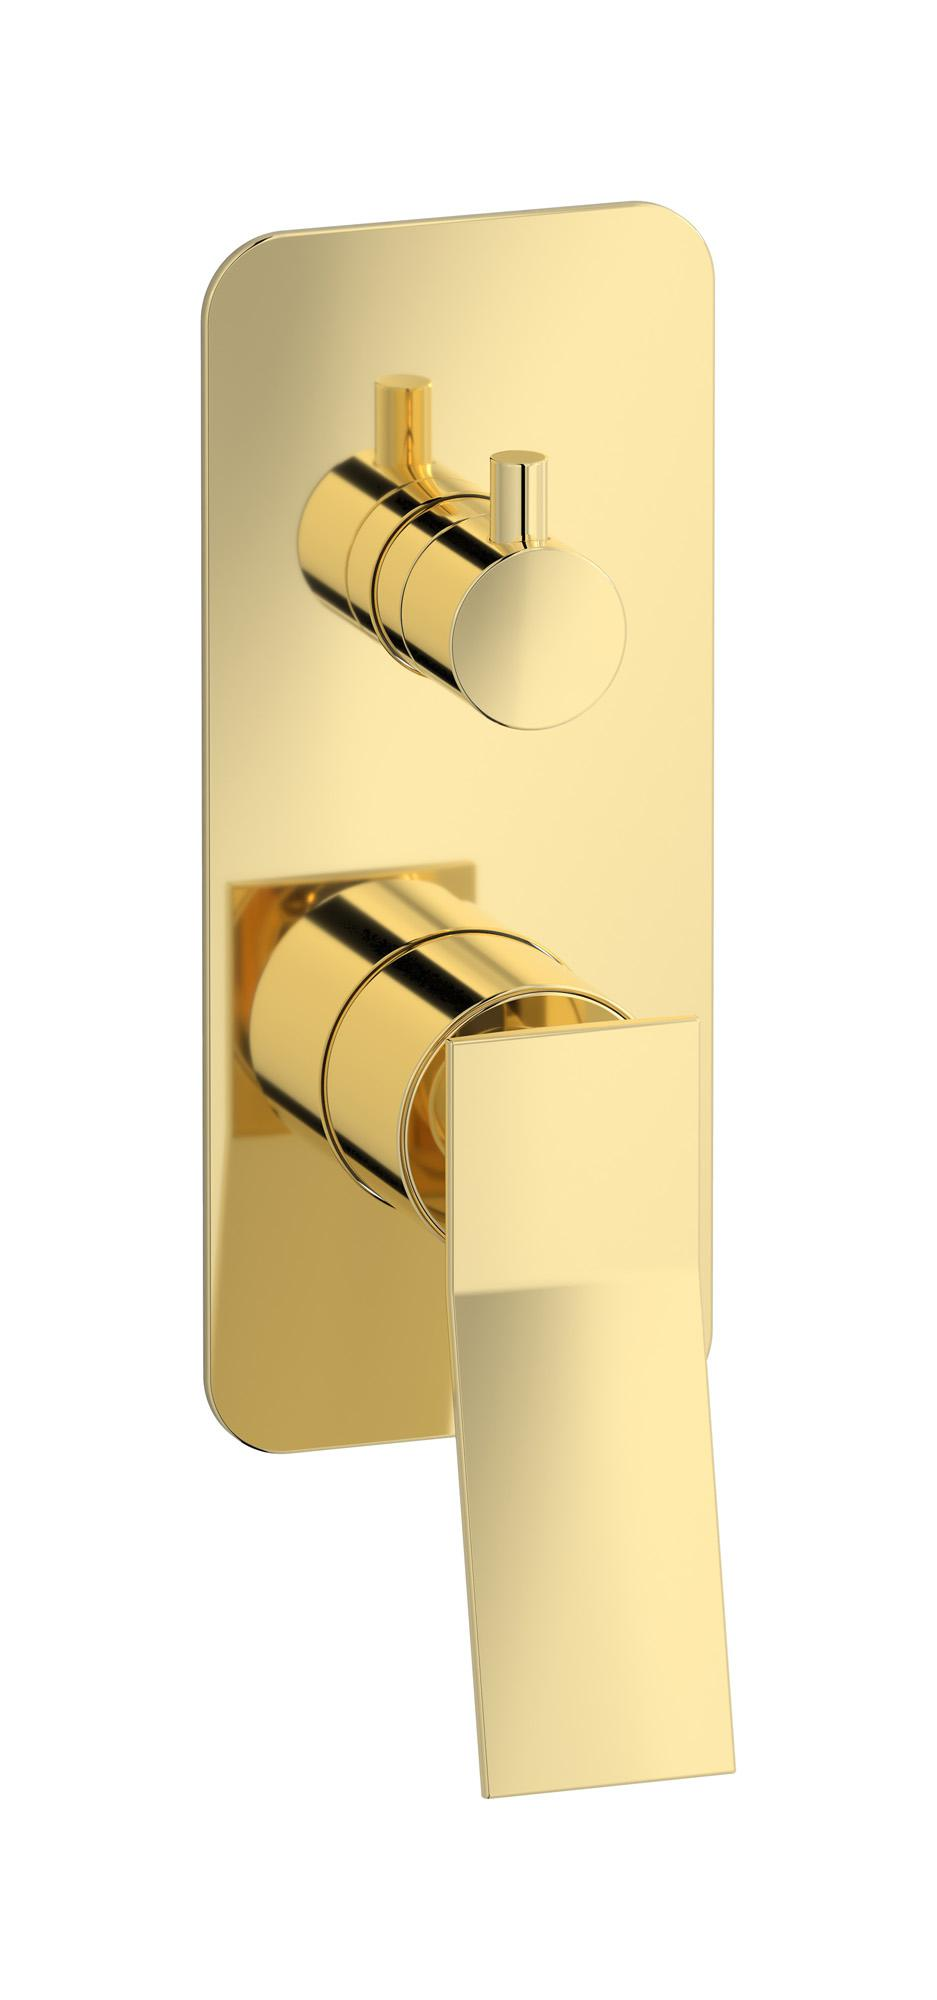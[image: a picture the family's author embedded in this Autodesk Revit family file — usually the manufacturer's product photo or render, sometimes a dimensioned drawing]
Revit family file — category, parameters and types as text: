
# Revit family: WA312
name_source: partatom
category: Apparecchi idraulici
units: mm (PartAtom-declared; Revit-internal decimal feet)

## family parameters
Basato su piano di lavoro = No
Condiviso = No
Mantieni orientamento annotazione = No
Numero OmniClass = 23.45.55.17
Punto di calcolo locali = No
Quota connettore circolare = Usa diametro
Sempre verticale = Sì
Taglio con vuoti quando caricato = No
Tipo di parte = Normale
Titolo OmniClass = Mixing Faucets

## types (12) — shared parameters
Cold water inlet = 10 mm  [stored 0.0328084 ft]
Commenti sul tipo = Wall mixer
Connessione CW = No
Connessione HW = No
Connessione di scarico = No
Connessione di ventilazione = No
Descrizione = Exposed parts for manual wall mixer with three ways diverter
Hot water inlet = 10 mm  [stored 0.0328084 ft]
Produttore = IB Rubinetterie S.p.A.
URL = https://www.weareib.it
zero-valued in all types: Prospetto di default

## per-type parameters (varying)
| type | Finishes surface | Immagine tipo | Modello |
| Chrome | IB_Chrome | WA312CC.jpg | WA312CC |
| Brushed nickel | IB_Brushed nickel | WA312SS.jpg | WA312SS |
| Matt white | IB_matt white | WA312BO.jpg | WA312BO |
| Matt black | IB_matt black | WA312NP.jpg | WA312NP |
| Black chrome | IB_Black chrome | WA312CF.jpg | WA312CF |
| Brushed black chrome | IB_Brushed black chrome | WA312CS.jpg | WA312CS |
| Pale gold | IB_Pale gold | WA312II.jpg | WA312II |
| Brushed pale gold | IB_brushed pale gold | WA312IS.jpg | WA312IS |
| Rose gold | IB_Rose gold | WA312RS.jpg | WA312RS |
| Brushed rose gold | IB_Brushed rose gold | WA312SR.jpg | WA312SR |
| Gold | IB_gold | WA312OO.jpg | WA312OO |
| Brushed gold | IB_brushed gold | WA312OS.jpg | WA312OS |

note: [stored X ft] marks values corroborated as IEEE doubles in the binary element streams (Revit-internal decimal feet)
